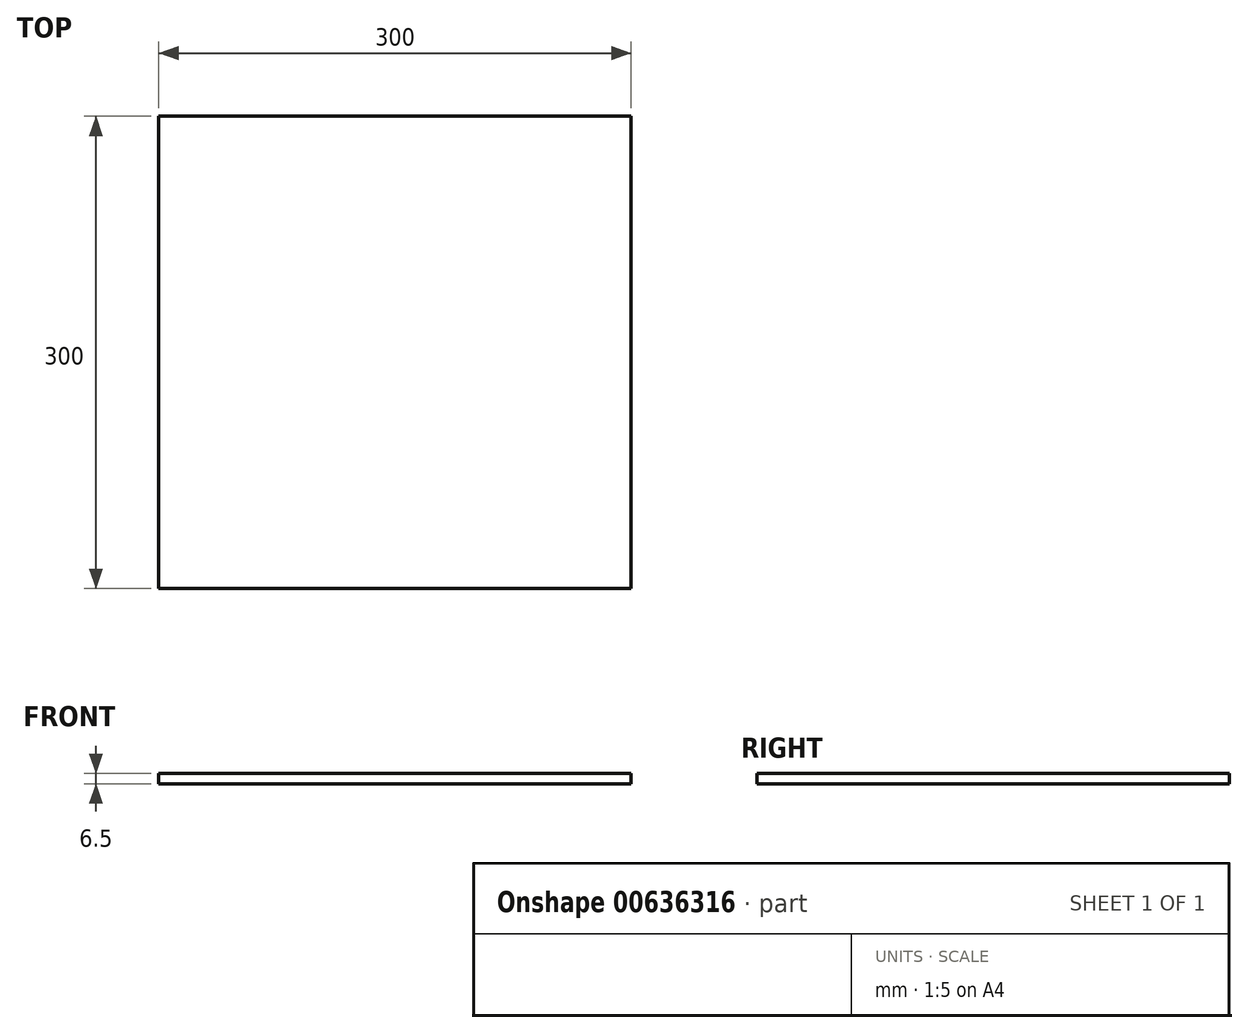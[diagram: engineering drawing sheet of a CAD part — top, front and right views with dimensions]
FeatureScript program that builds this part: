
annotation { "Feature Type Name" : "Feature", "Feature Type Description" : "" }
export const myFeature = defineFeature(function(context is Context, id is Id, definition is map)
    precondition{}
    {
        {
            var Q0;
            Q0=qCreatedBy(makeId("Top.planeOp"),FACE);
            var sketch = newSketch(context, id + "F0", { "sketchPlane" : qUnion([Q0])});
            skLineSegment(sketch, "E0.bottom", {"start": v(150, -150) * mm, "end": v(-150, -150) * mm});
            skLineSegment(sketch, "E0.top", {"start": v(150, 150) * mm, "end": v(-150, 150) * mm});
            skLineSegment(sketch, "E0.left", {"start": v(150, -150) * mm, "end": v(150, 150) * mm});
            skLineSegment(sketch, "E0.right", {"start": v(-150, -150) * mm, "end": v(-150, 150) * mm});
            skSolve(sketch);
        }
        {
            var Q0;
            Q0 = qSketchRegion(id + "F0", true);
            extrude(context, id + "F1", {"entities" : qUnion([Q0]), "depth" : 6.5 * mm, "offsetDistance" : 25 * mm});
        }
    });
